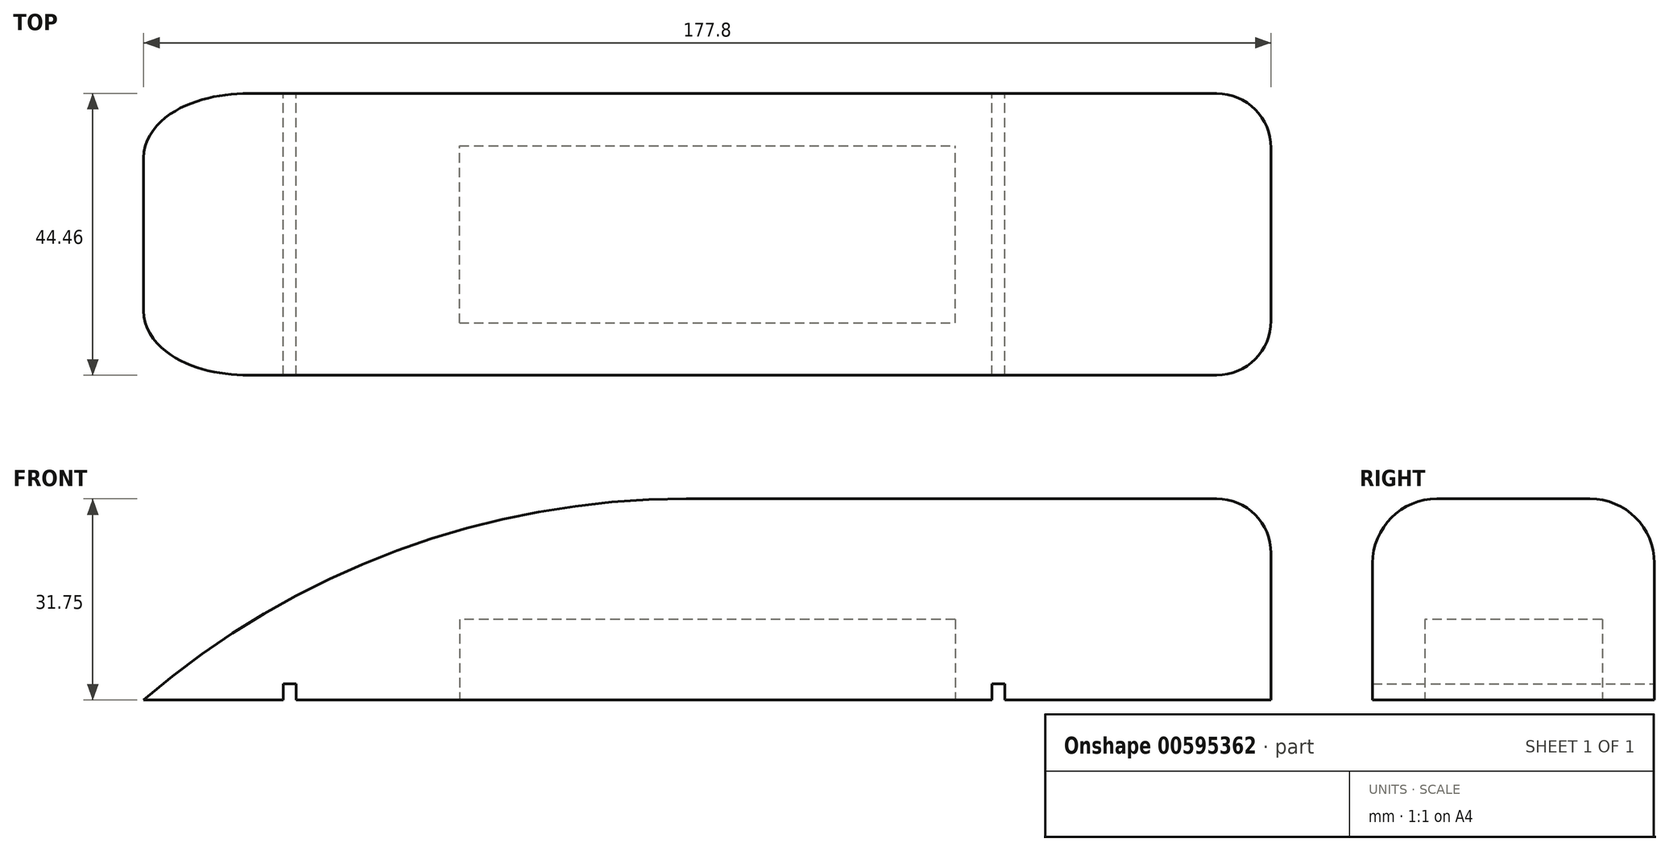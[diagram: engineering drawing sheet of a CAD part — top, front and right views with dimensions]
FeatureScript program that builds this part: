
annotation { "Feature Type Name" : "Feature", "Feature Type Description" : "" }
export const myFeature = defineFeature(function(context is Context, id is Id, definition is map)
    precondition{}
    {
        {
            var Q0;
            Q0=qCreatedBy(makeId("Top.planeOp"),FACE);
            var sketch = newSketch(context, id + "F0", { "sketchPlane" : qUnion([Q0])});
            skLineSegment(sketch, "E0.bottom", {"start": v(88.9, -22.22) * mm, "end": v(-88.9, -22.23) * mm});
            skLineSegment(sketch, "E0.top", {"start": v(88.9, 22.23) * mm, "end": v(-88.9, 22.22) * mm});
            skLineSegment(sketch, "E0.left", {"start": v(88.9, -22.22) * mm, "end": v(88.9, 22.23) * mm});
            skLineSegment(sketch, "E0.right", {"start": v(-88.9, -22.23) * mm, "end": v(-88.9, 22.22) * mm});
            skPoint(sketch, "E0.middle", {"position": v(0, 0) * mm});
            skSolve(sketch);
        }
        {
            var Q0;
            Q0=makeQuery(id+"F0.imprint","IMPRINT",FACE,{"disambiguationData":[TD([[makeQuery(id+"F0.imprint","IMPRINT",EDGE,{"derivedFrom":sQuery(id+"F0.wireOp",EDGE,"E0.bottom")}),-1.0]])]});
            extrude(context, id + "F1", {"entities" : qUnion([Q0]), "depth" : 31.75 * mm});
        }
        {
            var Q0;
            Q0=qCreatedBy(makeId("Front.planeOp"),FACE);
            var sketch = newSketch(context, id + "F2", { "sketchPlane" : qUnion([Q0])});
            skLineSegment(sketch, "E1.bottom", {"start": v(-64.87, 2.54) * mm, "end": v(-66.9, 2.54) * mm});
            skLineSegment(sketch, "E1.top", {"start": v(-64.87, -2.54) * mm, "end": v(-66.9, -2.54) * mm});
            skLineSegment(sketch, "E1.left", {"start": v(-64.87, 2.54) * mm, "end": v(-64.87, -2.54) * mm});
            skLineSegment(sketch, "E1.right", {"start": v(-66.9, 2.54) * mm, "end": v(-66.9, -2.54) * mm});
            skPoint(sketch, "E1.middle", {"position": v(-65.89, 0) * mm});
            skLineSegment(sketch, "E2.bottom", {"start": v(46.89, 2.54) * mm, "end": v(44.86, 2.54) * mm});
            skLineSegment(sketch, "E2.top", {"start": v(46.89, -0.42) * mm, "end": v(44.86, -0.42) * mm});
            skLineSegment(sketch, "E2.left", {"start": v(46.89, 2.54) * mm, "end": v(46.89, -0.42) * mm});
            skLineSegment(sketch, "E2.right", {"start": v(44.86, 2.54) * mm, "end": v(44.86, -0.42) * mm});
            skPoint(sketch, "E2.middle", {"position": v(45.87, 1.06) * mm});
            skSolve(sketch);
        }
        {
            var Q0;
            Q0=makeQuery(id+"F2.imprint","IMPRINT",FACE,{"disambiguationData":[TD([[makeQuery(id+"F2.imprint","IMPRINT",EDGE,{"derivedFrom":sQuery(id+"F2.wireOp",EDGE,"E1.bottom")}),1.0]])]});
            var Q1;
            Q1=makeQuery(id+"F2.imprint","IMPRINT",FACE,{"disambiguationData":[TD([[makeQuery(id+"F2.imprint","IMPRINT",EDGE,{"derivedFrom":sQuery(id+"F2.wireOp",EDGE,"E2.bottom")}),1.0]])]});
            extrude(context, id + "F3", {"entities" : qUnion([Q0, Q1]), "operationType" : NewBodyOperationType.REMOVE, "endBound" : BoundingType.SYMMETRIC, "depth" : 141.73 * mm, "offsetDistance" : 25.4 * mm});
        }
        {
            var Q0;
            Q0=makeQuery(id+"F1.opExtrude","CAP_EDGE",EDGE,{"disambiguationData":[OSD([sQuery(id+"F0.wireOp",EDGE,"E0.right")])],"isStart":false});
            fillet(context, id + "F4", {"entities" : qUnion([Q0]), "radius" : 131.23 * mm, "tangentPropagation" : true, "allowEdgeOverflow" : false});
        }
        {
            var Q0;
            Q0=makeQuery(id+"F4.opFillet","BLEND_EDGE",EDGE,{"blendedFrom":[makeQuery(id+"F1.opExtrude","CAP_EDGE",EDGE,{"disambiguationData":[OSD([sQuery(id+"F0.wireOp",EDGE,"E0.right")])],"isStart":false}),makeQuery(id+"F1.opExtrude","SWEPT_FACE",FACE,{"disambiguationData":[OSD([sQuery(id+"F0.wireOp",EDGE,"E0.bottom")])]})],"blendedInto":[makeQuery(id+"F1.opExtrude","SWEPT_FACE",FACE,{"disambiguationData":[OSD([sQuery(id+"F0.wireOp",EDGE,"E0.bottom")])]})]});
            fillet(context, id + "F5", {"entities" : qUnion([Q0]), "radius" : 10.16 * mm, "tangentPropagation" : true, "allowEdgeOverflow" : false});
        }
        {
            var Q0;
            Q0=makeQuery(id+"F1.opExtrude","CAP_EDGE",EDGE,{"disambiguationData":[OSD([sQuery(id+"F0.wireOp",EDGE,"E0.top")])],"isStart":false});
            fillet(context, id + "F6", {"entities" : qUnion([Q0]), "radius" : 10.16 * mm, "tangentPropagation" : true, "allowEdgeOverflow" : false});
        }
        {
            var Q0;
            Q0=makeQuery(id+"F1.opExtrude","CAP_EDGE",EDGE,{"disambiguationData":[OSD([sQuery(id+"F0.wireOp",EDGE,"E0.left")])],"isStart":false});
            fillet(context, id + "F7", {"entities" : qUnion([Q0]), "radius" : 8.58 * mm, "tangentPropagation" : true, "allowEdgeOverflow" : false});
        }
        {
            var Q0;
            Q0=qCreatedBy(makeId("Top.planeOp"),FACE);
            var sketch = newSketch(context, id + "F8", { "sketchPlane" : qUnion([Q0])});
            skLineSegment(sketch, "E3.bottom", {"start": v(39.09, 14) * mm, "end": v(-39.09, 14) * mm});
            skLineSegment(sketch, "E3.top", {"start": v(39.09, -14) * mm, "end": v(-39.09, -14) * mm});
            skLineSegment(sketch, "E3.left", {"start": v(39.09, 14) * mm, "end": v(39.09, -14) * mm});
            skLineSegment(sketch, "E3.right", {"start": v(-39.09, 14) * mm, "end": v(-39.09, -14) * mm});
            skPoint(sketch, "E3.middle", {"position": v(0, 0) * mm});
            skSolve(sketch);
        }
        {
            var Q0;
            Q0=makeQuery(id+"F8.imprint","IMPRINT",FACE,{"disambiguationData":[TD([[makeQuery(id+"F8.imprint","IMPRINT",EDGE,{"derivedFrom":sQuery(id+"F8.wireOp",EDGE,"E3.bottom")}),1.0]])]});
            extrude(context, id + "F9", {"entities" : qUnion([Q0]), "operationType" : NewBodyOperationType.REMOVE, "endBound" : BoundingType.SYMMETRIC, "depth" : 25.4 * mm, "offsetDistance" : 25.4 * mm});
        }
    });
